FCSTD DOCUMENT  (FreeCAD 1.0R39109 (Git))
Label: PVC_limit
License: All rights reserved
LicenseURL: https://en.wikipedia.org/wiki/All_rights_reserved
objects: Sketcher::SketchObject×1, PartDesign::Body×1
note: 3 computed .brp shape members not serialized (recipe doc carries the construction recipe); baked Part::Feature solids carry a one-line shape summary decoded from their .brp

FEATURE [Sketcher::SketchObject] Sketch
  ArcFitTolerance = 1e-06
  AttachmentSupport = -> [XY_Plane]
  FullyConstrained = true
  MakeInternals = false
  MapMode = 5
  sketch-geometry (69):
    g0: LineSegment StartX=2 StartY=0 StartZ=0 EndX=28 EndY=0 EndZ=0
    g1: LineSegment StartX=30 StartY=2 StartZ=0 EndX=30 EndY=198 EndZ=0
    g2: LineSegment StartX=28 StartY=200 StartZ=0 EndX=2 EndY=200 EndZ=0
    g3: LineSegment StartX=0 StartY=198 StartZ=0 EndX=0 EndY=2 EndZ=0
    g4: Circle [constr] CenterX=15 CenterY=20 CenterZ=0 NormalX=0 NormalY=0 NormalZ=1 AngleXU=0 Radius=1.5
    g5: Circle [constr] CenterX=25 CenterY=20 CenterZ=0 NormalX=0 NormalY=0 NormalZ=1 AngleXU=0 Radius=1.5
    g6: Circle [constr] CenterX=5 CenterY=20 CenterZ=0 NormalX=0 NormalY=0 NormalZ=1 AngleXU=0 Radius=1.5
    g7: Circle [constr] CenterX=15 CenterY=30 CenterZ=0 NormalX=0 NormalY=0 NormalZ=1 AngleXU=0 Radius=1.5
    g8: Circle [constr] CenterX=25 CenterY=30 CenterZ=0 NormalX=0 NormalY=0 NormalZ=1 AngleXU=0 Radius=1.5
    g9: Circle [constr] CenterX=5 CenterY=30 CenterZ=0 NormalX=0 NormalY=0 NormalZ=1 AngleXU=0 Radius=1.5
    g10: Circle [constr] CenterX=15 CenterY=40 CenterZ=0 NormalX=0 NormalY=0 NormalZ=1 AngleXU=0 Radius=1.5
    g11: Circle [constr] CenterX=25 CenterY=40 CenterZ=0 NormalX=0 NormalY=0 NormalZ=1 AngleXU=0 Radius=1.5
    g12: Circle [constr] CenterX=5 CenterY=40 CenterZ=0 NormalX=0 NormalY=0 NormalZ=1 AngleXU=0 Radius=1.5
    g13: Circle [constr] CenterX=15 CenterY=50 CenterZ=0 NormalX=0 NormalY=0 NormalZ=1 AngleXU=0 Radius=1.5
    g14: Circle [constr] CenterX=25 CenterY=50 CenterZ=0 NormalX=0 NormalY=0 NormalZ=1 AngleXU=0 Radius=1.5
    g15: Circle [constr] CenterX=5 CenterY=50 CenterZ=0 NormalX=0 NormalY=0 NormalZ=1 AngleXU=0 Radius=1.5
    g16: Circle [constr] CenterX=15 CenterY=70 CenterZ=0 NormalX=0 NormalY=0 NormalZ=1 AngleXU=0 Radius=1.5
    g17: Circle CenterX=25 CenterY=70 CenterZ=0 NormalX=0 NormalY=0 NormalZ=1 AngleXU=0 Radius=1.5
    g18: Circle CenterX=5 CenterY=70 CenterZ=0 NormalX=0 NormalY=0 NormalZ=1 AngleXU=0 Radius=1.5
    g19: Circle [constr] CenterX=15 CenterY=10 CenterZ=0 NormalX=0 NormalY=0 NormalZ=1 AngleXU=0 Radius=1.5
    g20: Circle [constr] CenterX=25 CenterY=10 CenterZ=0 NormalX=0 NormalY=0 NormalZ=1 AngleXU=0 Radius=1.5
    g21: Circle [constr] CenterX=5 CenterY=10 CenterZ=0 NormalX=0 NormalY=0 NormalZ=1 AngleXU=0 Radius=1.5
    g22: Circle [constr] CenterX=15 CenterY=80 CenterZ=0 NormalX=0 NormalY=0 NormalZ=1 AngleXU=0 Radius=1.5
    g23: Circle CenterX=25 CenterY=80 CenterZ=0 NormalX=0 NormalY=0 NormalZ=1 AngleXU=0 Radius=1.5
    g24: Circle CenterX=5 CenterY=80 CenterZ=0 NormalX=0 NormalY=0 NormalZ=1 AngleXU=0 Radius=1.5
    g25: Circle [constr] CenterX=15 CenterY=90 CenterZ=0 NormalX=0 NormalY=0 NormalZ=1 AngleXU=0 Radius=1.5
    g26: Circle CenterX=25 CenterY=90 CenterZ=0 NormalX=0 NormalY=0 NormalZ=1 AngleXU=0 Radius=1.5
    g27: Circle CenterX=5 CenterY=90 CenterZ=0 NormalX=0 NormalY=0 NormalZ=1 AngleXU=0 Radius=1.5
    g28: Circle [constr] CenterX=15 CenterY=150 CenterZ=0 NormalX=0 NormalY=0 NormalZ=1 AngleXU=0 Radius=1.5
    g29: Circle [constr] CenterX=25 CenterY=150 CenterZ=0 NormalX=0 NormalY=0 NormalZ=1 AngleXU=0 Radius=1.5
    g30: Circle [constr] CenterX=5 CenterY=150 CenterZ=0 NormalX=0 NormalY=0 NormalZ=1 AngleXU=0 Radius=1.5
    g31: Circle [constr] CenterX=15 CenterY=60 CenterZ=0 NormalX=0 NormalY=0 NormalZ=1 AngleXU=0 Radius=1.5
    g32: Circle CenterX=25 CenterY=60 CenterZ=0 NormalX=0 NormalY=0 NormalZ=1 AngleXU=0 Radius=1.5
    g33: Circle CenterX=5 CenterY=60 CenterZ=0 NormalX=0 NormalY=0 NormalZ=1 AngleXU=0 Radius=1.5
    g34: Circle [constr] CenterX=15 CenterY=170 CenterZ=0 NormalX=0 NormalY=0 NormalZ=1 AngleXU=0 Radius=1.5
    g35: Circle [constr] CenterX=25 CenterY=170 CenterZ=0 NormalX=0 NormalY=0 NormalZ=1 AngleXU=0 Radius=1.5
    g36: Circle [constr] CenterX=5 CenterY=170 CenterZ=0 NormalX=0 NormalY=0 NormalZ=1 AngleXU=0 Radius=1.5
    g37: Circle [constr] CenterX=15 CenterY=100 CenterZ=0 NormalX=0 NormalY=0 NormalZ=1 AngleXU=0 Radius=1.5
    g38: Circle CenterX=25 CenterY=100 CenterZ=0 NormalX=0 NormalY=0 NormalZ=1 AngleXU=0 Radius=1.5
    g39: Circle CenterX=5 CenterY=100 CenterZ=0 NormalX=0 NormalY=0 NormalZ=1 AngleXU=0 Radius=1.5
    g40: Circle [constr] CenterX=15 CenterY=110 CenterZ=0 NormalX=0 NormalY=0 NormalZ=1 AngleXU=0 Radius=1.5
    g41: Circle CenterX=25 CenterY=110 CenterZ=0 NormalX=0 NormalY=0 NormalZ=1 AngleXU=0 Radius=1.5
    g42: Circle CenterX=5 CenterY=110 CenterZ=0 NormalX=0 NormalY=0 NormalZ=1 AngleXU=0 Radius=1.5
    g43: Circle [constr] CenterX=15 CenterY=180 CenterZ=0 NormalX=0 NormalY=0 NormalZ=1 AngleXU=0 Radius=1.5
    g44: Circle [constr] CenterX=25 CenterY=180 CenterZ=0 NormalX=0 NormalY=0 NormalZ=1 AngleXU=0 Radius=1.5
    g45: Circle [constr] CenterX=5 CenterY=180 CenterZ=0 NormalX=0 NormalY=0 NormalZ=1 AngleXU=0 Radius=1.5
    g46: Circle [constr] CenterX=15 CenterY=160 CenterZ=0 NormalX=0 NormalY=0 NormalZ=1 AngleXU=0 Radius=1.5
    g47: Circle [constr] CenterX=25 CenterY=160 CenterZ=0 NormalX=0 NormalY=0 NormalZ=1 AngleXU=0 Radius=1.5
    g48: Circle [constr] CenterX=5 CenterY=160 CenterZ=0 NormalX=0 NormalY=0 NormalZ=1 AngleXU=0 Radius=1.5
    g49: Circle [constr] CenterX=15 CenterY=120 CenterZ=0 NormalX=0 NormalY=0 NormalZ=1 AngleXU=0 Radius=1.5
    g50: Circle CenterX=25 CenterY=120 CenterZ=0 NormalX=0 NormalY=0 NormalZ=1 AngleXU=0 Radius=1.5
    g51: Circle CenterX=5 CenterY=120 CenterZ=0 NormalX=0 NormalY=0 NormalZ=1 AngleXU=0 Radius=1.5
    g52: Circle [constr] CenterX=15 CenterY=140 CenterZ=0 NormalX=0 NormalY=0 NormalZ=1 AngleXU=0 Radius=1.5
    g53: Circle CenterX=25 CenterY=140 CenterZ=0 NormalX=0 NormalY=0 NormalZ=1 AngleXU=0 Radius=1.5
    g54: Circle CenterX=5 CenterY=140 CenterZ=0 NormalX=0 NormalY=0 NormalZ=1 AngleXU=0 Radius=1.5
    g55: Circle [constr] CenterX=15 CenterY=190 CenterZ=0 NormalX=0 NormalY=0 NormalZ=1 AngleXU=0 Radius=1.5
    g56: Circle [constr] CenterX=25 CenterY=190 CenterZ=0 NormalX=0 NormalY=0 NormalZ=1 AngleXU=0 Radius=1.5
    g57: Circle [constr] CenterX=5 CenterY=190 CenterZ=0 NormalX=0 NormalY=0 NormalZ=1 AngleXU=0 Radius=1.5
    g58: Circle [constr] CenterX=15 CenterY=130 CenterZ=0 NormalX=0 NormalY=0 NormalZ=1 AngleXU=0 Radius=1.5
    g59: Circle CenterX=25 CenterY=130 CenterZ=0 NormalX=0 NormalY=0 NormalZ=1 AngleXU=0 Radius=1.5
    g60: Circle CenterX=5 CenterY=130 CenterZ=0 NormalX=0 NormalY=0 NormalZ=1 AngleXU=0 Radius=1.5
    g61: ArcOfCircle CenterX=2 CenterY=198 CenterZ=0 NormalX=0 NormalY=0 NormalZ=1 AngleXU=0 Radius=2 StartAngle=1.5708 EndAngle=3.14159
    g62: GeomPoint [constr] X=0 Y=200 Z=0
    g63: ArcOfCircle CenterX=28 CenterY=198 CenterZ=0 NormalX=0 NormalY=0 NormalZ=1 AngleXU=0 Radius=2 StartAngle=-6.2e-15 EndAngle=1.5708
    g64: GeomPoint [constr] X=30 Y=200 Z=0
    g65: ArcOfCircle CenterX=28 CenterY=2 CenterZ=0 NormalX=0 NormalY=0 NormalZ=1 AngleXU=0 Radius=2 StartAngle=4.71239 EndAngle=6.28319
    g66: GeomPoint [constr] X=30 Y=0 Z=0
    g67: ArcOfCircle CenterX=2 CenterY=2 CenterZ=0 NormalX=0 NormalY=0 NormalZ=1 AngleXU=0 Radius=2 StartAngle=3.14159 EndAngle=4.71239
    g68: GeomPoint [constr] X=0 Y=0 Z=0
  constraints (198):
    c: Horizontal(g0)
    c: Horizontal(g2)
    c: Vertical(g1)
    c: Vertical(g3)
    c: Distance(g66,g68) = 30
    c: Distance(g68,g62) = 200
    c: Coincident(g68,g-1)
    c: Diameter(g4) = 3
    c: Diameter(g5) = 3
    c: DistanceX(g4,g5) = 10
    c: DistanceX(g68,g4) = 15
    c: DistanceY(g5,g4) = 0
    c: Diameter(g6) = 3
    c: DistanceX(g6,g4) = 10
    c: DistanceY(g6,g4) = 0
    c: DistanceY(g68,g4) = 20
    c: Diameter(g7) = 3
    c: Diameter(g8) = 3
    c: DistanceX(g7,g8) = 10
    c: DistanceY(g8,g7) = 0
    c: Diameter(g9) = 3
    c: DistanceX(g9,g7) = 10
    c: DistanceY(g9,g7) = 0
    c: Diameter(g10) = 3
    c: Diameter(g11) = 3
    c: DistanceX(g10,g11) = 10
    c: DistanceY(g11,g10) = 0
    c: Diameter(g12) = 3
    c: DistanceX(g12,g10) = 10
    c: DistanceY(g12,g10) = 0
    c: Diameter(g13) = 3
    c: Diameter(g14) = 3
    c: DistanceX(g13,g14) = 10
    c: DistanceY(g14,g13) = 0
    c: Diameter(g15) = 3
    c: DistanceX(g15,g13) = 10
    c: DistanceY(g15,g13) = 0
    c: Diameter(g16) = 3
    c: Diameter(g17) = 3
    c: DistanceX(g16,g17) = 10
    c: DistanceY(g17,g16) = 0
    c: Diameter(g18) = 3
    c: DistanceX(g18,g16) = 10
    c: DistanceY(g18,g16) = 0
    c: Diameter(g19) = 3
    c: Diameter(g20) = 3
    c: DistanceX(g19,g20) = 10
    c: DistanceY(g20,g19) = 0
    c: Diameter(g21) = 3
    c: DistanceX(g21,g19) = 10
    c: DistanceY(g21,g19) = 0
    c: DistanceY(g68,g19) = 10
    c: DistanceX(g4,g19) = 0
    c: DistanceX(g4,g7) = 0
    c: DistanceX(g7,g10) = 0
    c: DistanceX(g10,g13) = 0
    c: Diameter(g22) = 3
    c: Diameter(g23) = 3
    c: DistanceX(g22,g23) = 10
    c: DistanceY(g23,g22) = 0
    c: Diameter(g24) = 3
    c: DistanceX(g24,g22) = 10
    c: DistanceY(g24,g22) = 0
    c: Diameter(g25) = 3
    c: Diameter(g26) = 3
    c: DistanceX(g25,g26) = 10
    c: DistanceY(g26,g25) = 0
    c: Diameter(g27) = 3
    c: DistanceX(g27,g25) = 10
    c: DistanceY(g27,g25) = 0
    c: Diameter(g28) = 3
    c: Diameter(g29) = 3
    c: DistanceX(g28,g29) = 10
    c: DistanceY(g29,g28) = 0
    c: Diameter(g30) = 3
    c: DistanceX(g30,g28) = 10
    c: DistanceY(g30,g28) = 0
    c: Diameter(g31) = 3
    c: Diameter(g32) = 3
    c: DistanceX(g31,g32) = 10
    c: DistanceY(g32,g31) = 0
    c: Diameter(g33) = 3
    c: DistanceX(g33,g31) = 10
    c: DistanceY(g33,g31) = 0
    c: Diameter(g34) = 3
    c: Diameter(g35) = 3
    c: DistanceX(g34,g35) = 10
    c: DistanceY(g35,g34) = 0
    c: Diameter(g36) = 3
    c: DistanceX(g36,g34) = 10
    c: DistanceY(g36,g34) = 0
    c: Diameter(g37) = 3
    c: Diameter(g38) = 3
    c: DistanceX(g37,g38) = 10
    c: DistanceY(g38,g37) = 0
    c: Diameter(g39) = 3
    c: DistanceX(g39,g37) = 10
    c: DistanceY(g39,g37) = 0
    c: Diameter(g40) = 3
    c: Diameter(g41) = 3
    c: DistanceX(g40,g41) = 10
    c: DistanceY(g41,g40) = 0
    c: Diameter(g42) = 3
    c: DistanceX(g42,g40) = 10
    c: DistanceY(g42,g40) = 0
    c: Diameter(g43) = 3
    c: Diameter(g44) = 3
    c: DistanceX(g43,g44) = 10
    c: DistanceY(g44,g43) = 0
    c: Diameter(g45) = 3
    c: DistanceX(g45,g43) = 10
    c: DistanceY(g45,g43) = 0
    c: Diameter(g46) = 3
    c: Diameter(g47) = 3
    c: DistanceX(g46,g47) = 10
    c: DistanceY(g47,g46) = 0
    c: Diameter(g48) = 3
    c: DistanceX(g48,g46) = 10
    c: DistanceY(g48,g46) = 0
    c: Diameter(g49) = 3
    c: Diameter(g50) = 3
    c: DistanceX(g49,g50) = 10
    c: DistanceY(g50,g49) = 0
    c: Diameter(g51) = 3
    c: DistanceX(g51,g49) = 10
    c: DistanceY(g51,g49) = 0
    c: Diameter(g52) = 3
    c: Diameter(g53) = 3
    c: DistanceX(g52,g53) = 10
    c: DistanceY(g53,g52) = 0
    c: Diameter(g54) = 3
    c: DistanceX(g54,g52) = 10
    c: DistanceY(g54,g52) = 0
    c: Diameter(g55) = 3
    c: Diameter(g56) = 3
    c: DistanceX(g55,g56) = 10
    c: DistanceY(g56,g55) = 0
    c: Diameter(g57) = 3
    c: DistanceX(g57,g55) = 10
    c: DistanceY(g57,g55) = 0
    c: Diameter(g58) = 3
    c: Diameter(g59) = 3
    c: DistanceX(g58,g59) = 10
    c: DistanceY(g59,g58) = 0
    c: Diameter(g60) = 3
    c: DistanceX(g60,g58) = 10
    c: DistanceY(g60,g58) = 0
    c: DistanceY(g4,g7) = 10
    c: DistanceY(g7,g10) = 10
    c: DistanceY(g10,g13) = 10
    c: DistanceY(g13,g31) = 10
    c: DistanceY(g16,g22) = 10
    c: DistanceY(g31,g16) = 10
    c: DistanceY(g22,g25) = 10
    c: DistanceY(g25,g37) = 10
    c: DistanceY(g37,g40) = 10
    c: DistanceY(g40,g49) = 10
    c: DistanceY(g49,g58) = 10
    c: DistanceY(g58,g52) = 10
    c: DistanceY(g52,g28) = 10
    c: DistanceY(g28,g46) = 10
    c: DistanceY(g46,g34) = 10
    c: DistanceY(g34,g43) = 10
    c: DistanceY(g43,g55) = 10
    c: DistanceX(g13,g31) = 0
    c: DistanceX(g31,g16) = 0
    c: DistanceX(g16,g22) = 0
    c: DistanceX(g22,g25) = 0
    c: DistanceX(g25,g37) = 0
    c: DistanceX(g37,g40) = 0
    c: DistanceX(g40,g49) = 0
    c: DistanceX(g49,g58) = 0
    c: DistanceX(g52,g58) = 0
    c: DistanceX(g28,g52) = 0
    c: DistanceX(g46,g28) = 0
    c: DistanceX(g34,g46) = 0
    c: DistanceX(g43,g34) = 0
    c: DistanceX(g55,g43) = 0
    c: PointOnObject(g62,g2)
    c: PointOnObject(g62,g3)
    c: Tangent(g2,g61) = -1.5708
    c: Tangent(g3,g61) = -1.5708
    c: PointOnObject(g64,g2)
    c: PointOnObject(g64,g1)
    c: Tangent(g2,g63) = -1.5708
    c: Tangent(g1,g63) = -1.5708
    c: PointOnObject(g66,g1)
    c: PointOnObject(g66,g0)
    c: Tangent(g1,g65) = -1.5708
    c: Tangent(g0,g65) = -1.5708
    c: PointOnObject(g68,g0)
    c: PointOnObject(g68,g3)
    c: Tangent(g0,g67) = -1.5708
    c: Tangent(g3,g67) = -1.5708
    c: DistanceX(g65,g66) = 2
    c: DistanceX(g68,g67) = 2
    c: DistanceX(g63,g64) = 2
    c: DistanceX(g62,g61) = 2
FEATURE [PartDesign::Body] Body
  AllowCompound = false
  Group = -> [Sketch]
  Origin = -> Origin
